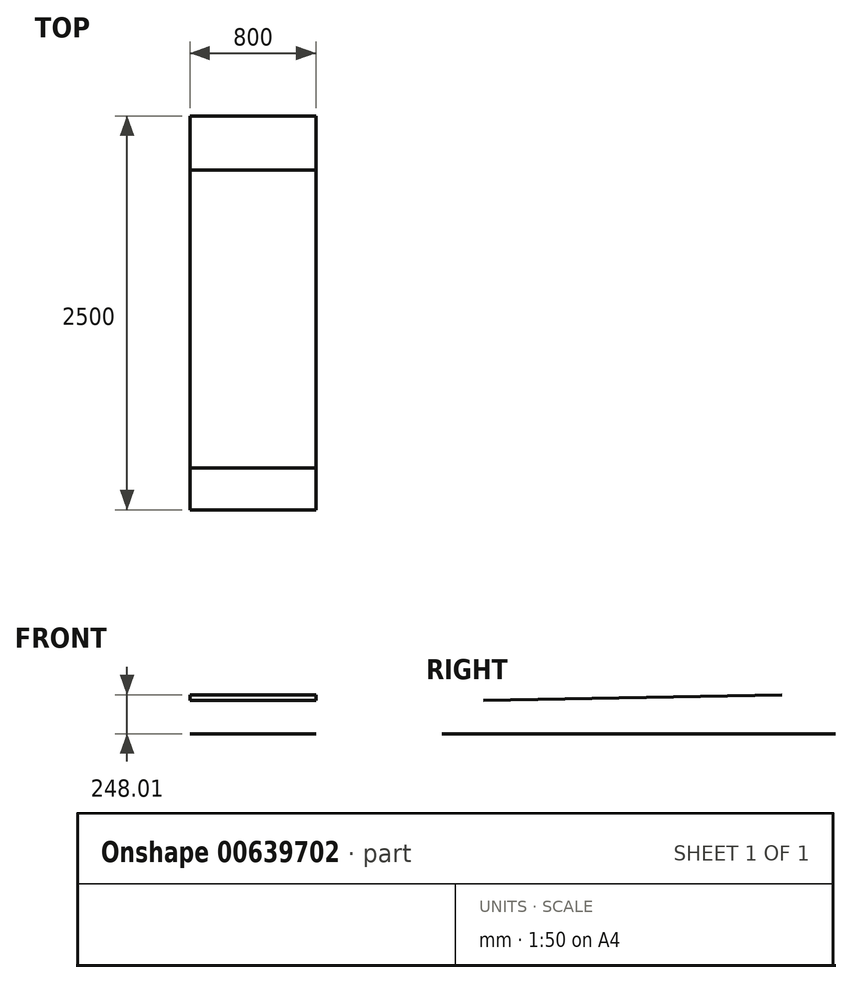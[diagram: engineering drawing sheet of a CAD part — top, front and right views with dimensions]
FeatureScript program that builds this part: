
annotation { "Feature Type Name" : "Feature", "Feature Type Description" : "" }
export const myFeature = defineFeature(function(context is Context, id is Id, definition is map)
    precondition{}
    {
        {
            var Q0;
            Q0=qCreatedBy(makeId("Right.planeOp"),FACE);
            var sketch = newSketch(context, id + "F0", { "sketchPlane" : qUnion([Q0])});
            skLineSegment(sketch, "E0.bottom", {"start": v(0, 0) * mm, "end": v(4500, 0) * mm});
            skLineSegment(sketch, "E0.top", {"start": v(0, 2063.85) * mm, "end": v(4500, 2063.85) * mm});
            skLineSegment(sketch, "E0.left", {"start": v(0, 0) * mm, "end": v(0, 2063.85) * mm});
            skLineSegment(sketch, "E0.right", {"start": v(4500, 0) * mm, "end": v(4500, 2063.85) * mm});
            skSolve(sketch);
        }
        {
            var Q0;
            Q0=qCreatedBy(makeId("Right.planeOp"),FACE);
            var sketch = newSketch(context, id + "F1", { "sketchPlane" : qUnion([Q0])});
            skLineSegment(sketch, "E1.bottom", {"start": v(1500, 0) * mm, "end": v(4000, 0) * mm});
            skLineSegment(sketch, "E1.top", {"start": v(1500, 2186.47) * mm, "end": v(4000, 2186.47) * mm});
            skLineSegment(sketch, "E1.left", {"start": v(1500, 0) * mm, "end": v(1500, 2186.47) * mm});
            skLineSegment(sketch, "E1.right", {"start": v(4000, 0) * mm, "end": v(4000, 2186.47) * mm});
            skLineSegment(sketch, "E2", {"start": v(3569.45, 1395.07) * mm, "end": v(3569.45, 247.06) * mm});
            skSolve(sketch);
        }
        {
            var Q0;
            Q0=qCreatedBy(makeId("Front.planeOp"),FACE);
            cPlane(context, id + "F2", {"entities" : qUnion([Q0]), "cplaneType" : CPlaneType.OFFSET, "offset" : 3569 * mm, "oppositeDirection" : true, "width" : 150 * mm, "height" : 150 * mm});
        }
        {
            var Q0;
            Q0=qCreatedBy(makeId("Right.planeOp"),FACE);
            var sketch = newSketch(context, id + "F3", { "sketchPlane" : qUnion([Q0])});
            skLineSegment(sketch, "E3", {"start": v(1763.75, 212.94) * mm, "end": v(3658.25, 248) * mm});
            skSolve(sketch);
        }
        {
            var Q0;
            Q0 = qSketchRegion(id + "F3", true);
            var Q1;
            Q1 = qConstructionFilter(qBodyType(qCreatedBy(id + "F3" ,EDGE), BodyType.WIRE), ConstructionObject.NO);
            var Q2;
            Q2=sQuery(id+"F1.wireOp",EDGE,"E1.bottom");
            extrude(context, id + "F4", {"entities" : qUnion([Q0]), "bodyType" : ToolBodyType.SURFACE, "surfaceEntities" : qUnion([Q1, Q2]), "endBound" : BoundingType.SYMMETRIC, "depth" : 800 * mm, "offsetDistance" : 25 * mm});
        }
    });
